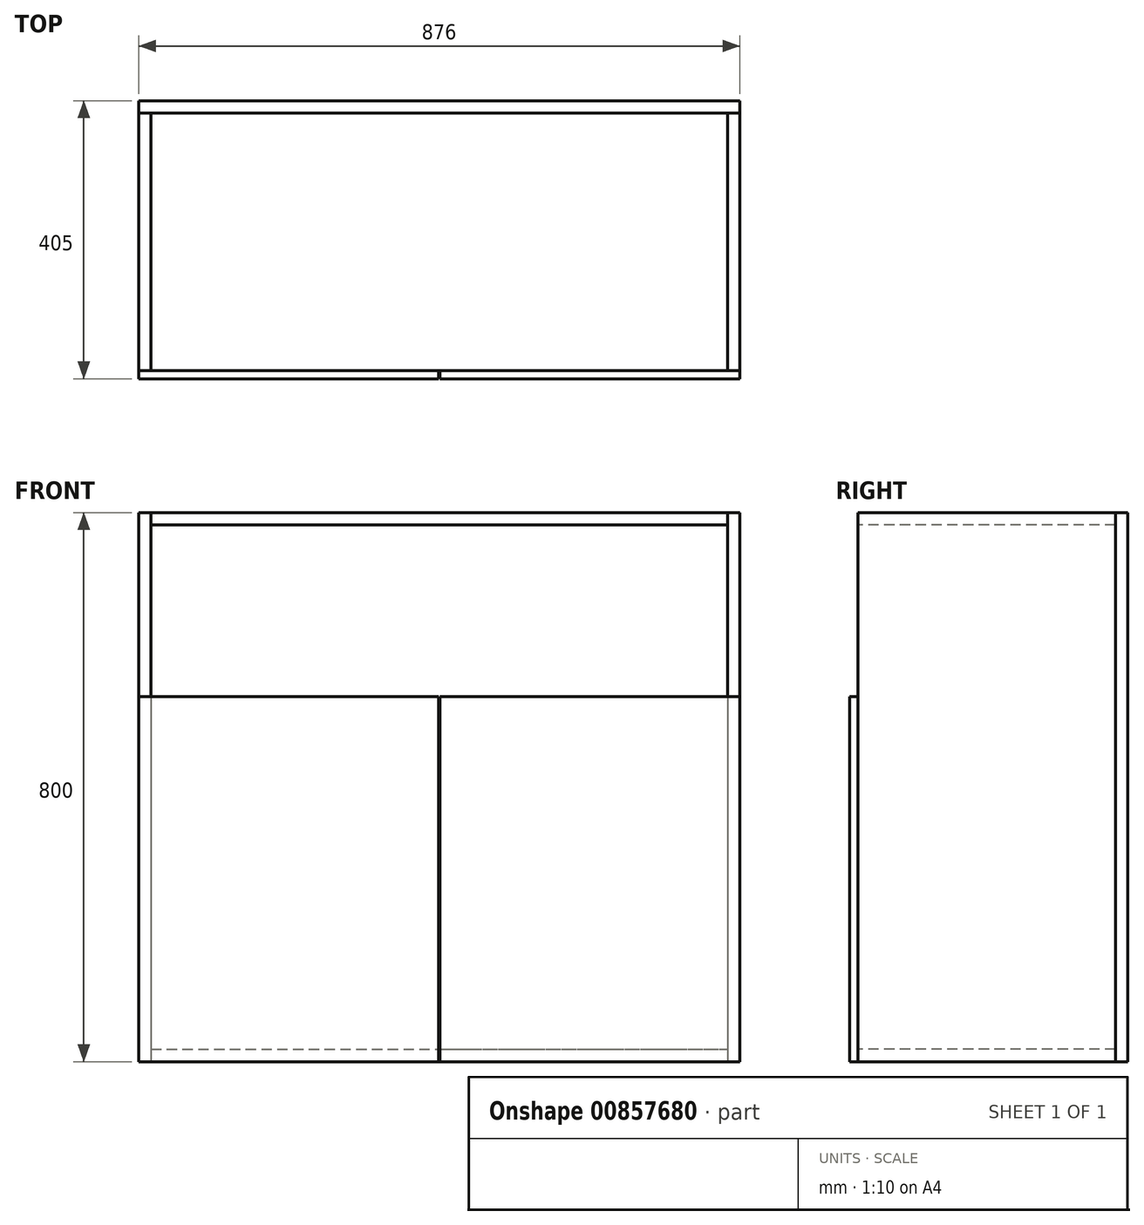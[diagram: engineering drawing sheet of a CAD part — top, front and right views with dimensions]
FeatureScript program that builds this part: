
annotation { "Feature Type Name" : "Feature", "Feature Type Description" : "" }
export const myFeature = defineFeature(function(context is Context, id is Id, definition is map)
    precondition{}
    {
        {
            var Q0;
            Q0=qCreatedBy(makeId("Top.planeOp"),FACE);
            var sketch = newSketch(context, id + "F0", { "sketchPlane" : qUnion([Q0])});
            skLineSegment(sketch, "E0.bottom", {"start": v(438, -187.5) * mm, "end": v(-438, -187.5) * mm});
            skLineSegment(sketch, "E0.top", {"start": v(438, 187.5) * mm, "end": v(-438, 187.5) * mm});
            skLineSegment(sketch, "E0.left", {"start": v(438, -187.5) * mm, "end": v(438, 187.5) * mm});
            skLineSegment(sketch, "E0.right", {"start": v(-438, -187.5) * mm, "end": v(-438, 187.5) * mm});
            skPoint(sketch, "E0.middle", {"position": v(0, 0) * mm});
            skLineSegment(sketch, "E1.0", {"start": v(420, 169.5) * mm, "end": v(-420, 169.5) * mm});
            skLineSegment(sketch, "E1.1", {"start": v(420, -169.5) * mm, "end": v(420, 169.5) * mm});
            skLineSegment(sketch, "E1.2", {"start": v(420, -169.5) * mm, "end": v(-420, -169.5) * mm});
            skLineSegment(sketch, "E1.3", {"start": v(-420, -169.5) * mm, "end": v(-420, 169.5) * mm});
            skLineSegment(sketch, "E2", {"start": v(-420, -169.5) * mm, "end": v(-420, -187.5) * mm});
            skLineSegment(sketch, "E3", {"start": v(-420, 169.5) * mm, "end": v(-420, 187.5) * mm});
            skLineSegment(sketch, "E4", {"start": v(420, 169.5) * mm, "end": v(420, 187.5) * mm});
            skLineSegment(sketch, "E5", {"start": v(420, -169.5) * mm, "end": v(420, -187.5) * mm});
            skSolve(sketch);
        }
        {
            var Q0;
            {var subQ0=sQuery(id+"F0.wireOp",EDGE,"E0.right");Q0=makeQuery(id+"F0.imprint","IMPRINT",FACE,{"disambiguationData":[TD([[makeQuery(id+"F0.imprint","IMPRINT",EDGE,{"derivedFrom":subQ0}),-1.0]])]});}
            var Q1;
            {var subQ0=sQuery(id+"F0.wireOp",EDGE,"E0.left");Q1=makeQuery(id+"F0.imprint","IMPRINT",FACE,{"disambiguationData":[TD([[makeQuery(id+"F0.imprint","IMPRINT",EDGE,{"derivedFrom":subQ0}),1.0]])]});}
            extrude(context, id + "F1", {"entities" : qUnion([Q0, Q1]), "depth" : 800 * mm, "offsetDistance" : 25 * mm});
        }
        {
            var Q0;
            Q0=makeQuery(id+"F1.opExtrude","CAP_FACE",FACE,{"disambiguationData":[OSD([sQuery(id+"F0.wireOp",EDGE,"E0.bottom"),sQuery(id+"F0.wireOp",EDGE,"E0.top"),sQuery(id+"F0.wireOp",EDGE,"E0.right"),sQuery(id+"F0.wireOp",EDGE,"E1.3"),sQuery(id+"F0.wireOp",EDGE,"E2"),sQuery(id+"F0.wireOp",EDGE,"E3")])],"isStart":false});
            var sketch = newSketch(context, id + "F2", { "sketchPlane" : qUnion([Q0])});
            skLineSegment(sketch, "E6.bottom", {"start": v(-420, -187.5) * mm, "end": v(420, -187.5) * mm});
            skLineSegment(sketch, "E6.top", {"start": v(-420, 187.5) * mm, "end": v(420, 187.5) * mm});
            skLineSegment(sketch, "E6.left", {"start": v(-420, -187.5) * mm, "end": v(-420, 187.5) * mm});
            skLineSegment(sketch, "E6.right", {"start": v(420, -187.5) * mm, "end": v(420, 187.5) * mm});
            skSolve(sketch);
        }
        {
            var Q0;
            Q0=makeQuery(id+"F2.imprint","IMPRINT",FACE,{"disambiguationData":[TD([[makeQuery(id+"F2.imprint","IMPRINT",EDGE,{"derivedFrom":sQuery(id+"F2.wireOp",EDGE,"E6.bottom")}),1.0]])]});
            extrude(context, id + "F3", {"entities" : qUnion([Q0]), "oppositeDirection" : true, "depth" : 18 * mm, "offsetDistance" : 25 * mm});
        }
        {
            var Q0;
            {var subQ0=sQuery(id+"F0.wireOp",EDGE,"E0.right");Q0=makeQuery(id+"F0.imprint","IMPRINT",FACE,{"disambiguationData":[TD([[makeQuery(id+"F0.imprint","IMPRINT",EDGE,{"derivedFrom":subQ0}),-1.0]])]});}
            var sketch = newSketch(context, id + "F4", { "sketchPlane" : qUnion([Q0])});
            skLineSegment(sketch, "E7.bottom", {"start": v(-420, -187.5) * mm, "end": v(420, -187.5) * mm});
            skLineSegment(sketch, "E7.top", {"start": v(-420, 187.5) * mm, "end": v(420, 187.5) * mm});
            skLineSegment(sketch, "E7.left", {"start": v(-420, -187.5) * mm, "end": v(-420, 187.5) * mm});
            skLineSegment(sketch, "E7.right", {"start": v(420, -187.5) * mm, "end": v(420, 187.5) * mm});
            skSolve(sketch);
        }
        {
            var Q0;
            {var subQ6=sQuery(id+"F4.wireOp",EDGE,"E7.bottom");Q0=makeQuery(id+"F4.imprint","IMPRINT",FACE,{"disambiguationData":[TD([[makeQuery(id+"F4.imprint","IMPRINT",EDGE,{"derivedFrom":subQ6}),1.0]])]});}
            extrude(context, id + "F5", {"entities" : qUnion([Q0]), "depth" : 18 * mm, "offsetDistance" : 25 * mm});
        }
        {
            var Q0;
            Q0=makeQuery(id+"F3.opExtrude","SWEPT_FACE",FACE,{"disambiguationData":[OSD([sQuery(id+"F2.wireOp",EDGE,"E6.top")])]});
            var sketch = newSketch(context, id + "F6", { "sketchPlane" : qUnion([Q0])});
            skLineSegment(sketch, "E8.bottom", {"start": v(-438, 800) * mm, "end": v(438, 800) * mm});
            skLineSegment(sketch, "E8.top", {"start": v(-438, 0) * mm, "end": v(438, 0) * mm});
            skLineSegment(sketch, "E8.left", {"start": v(-438, 800) * mm, "end": v(-438, 0) * mm});
            skLineSegment(sketch, "E8.right", {"start": v(438, 800) * mm, "end": v(438, 0) * mm});
            skSolve(sketch);
        }
        {
            var Q0;
            Q0=makeQuery(id+"F6.imprint","IMPRINT",FACE,{"disambiguationData":[TD([[makeQuery(id+"F6.imprint","IMPRINT",EDGE,{"derivedFrom":sQuery(id+"F6.wireOp",EDGE,"E8.top")}),1.0]])]});
            var Q1;
            {var subQ1=sQuery(id+"F2.wireOp",EDGE,"E6.top");Q1=makeQuery(id+"F6.imprint","IMPRINT",FACE,{"disambiguationData":[TD([[makeQuery(id+"F6.imprint","IMPRINT",EDGE,{"derivedFrom":makeQuery(id+"F3.opExtrude","CAP_EDGE",EDGE,{"disambiguationData":[OSD([subQ1])],"isStart":false})}),-1.0]])]});}
            extrude(context, id + "F7", {"entities" : qUnion([Q0, Q1]), "depth" : 18 * mm, "offsetDistance" : 25 * mm});
        }
        {
            var Q0;
            {var subQ0=sQuery(id+"F0.wireOp",EDGE,"E0.bottom");Q0=makeQuery(id+"F1.opExtrude","SWEPT_FACE",FACE,{"disambiguationData":[OSD([subQ0]),TDD([makeQuery(id+"F0.imprint","IMPRINT",EDGE,{"disambiguationData":[TD([[makeQuery(id+"F0.imprint","INTERSECT",VERTEX,{"derivedFrom":[subQ0,sQuery(id+"F0.wireOp",EDGE,"E0.right")]}),1.0]])],"derivedFrom":subQ0})])]});}
            var sketch = newSketch(context, id + "F8", { "sketchPlane" : qUnion([Q0])});
            skLineSegment(sketch, "E9.bottom", {"start": v(-438, 0) * mm, "end": v(-1, 0) * mm});
            skLineSegment(sketch, "E9.top", {"start": v(-438, 532) * mm, "end": v(-1, 532) * mm});
            skLineSegment(sketch, "E9.left", {"start": v(-438, 0) * mm, "end": v(-438, 532) * mm});
            skLineSegment(sketch, "E9.right", {"start": v(-1, 0) * mm, "end": v(-1, 532) * mm});
            skLineSegment(sketch, "E10.bottom", {"start": v(438, 0) * mm, "end": v(1, 0) * mm});
            skLineSegment(sketch, "E10.top", {"start": v(438, 532) * mm, "end": v(1, 532) * mm});
            skLineSegment(sketch, "E10.left", {"start": v(438, 0) * mm, "end": v(438, 532) * mm});
            skLineSegment(sketch, "E10.right", {"start": v(1, 0) * mm, "end": v(1, 532) * mm});
            skSolve(sketch);
        }
        {
            var Q0;
            {var subQ3=sQuery(id+"F8.wireOp",EDGE,"E9.right");Q0=makeQuery(id+"F8.imprint","IMPRINT",FACE,{"disambiguationData":[TD([[makeQuery(id+"F8.imprint","IMPRINT",EDGE,{"derivedFrom":subQ3}),1.0]])]});}
            var Q1;
            {var subQ0=sQuery(id+"F8.wireOp",EDGE,"E9.left");Q1=makeQuery(id+"F8.imprint","IMPRINT",FACE,{"disambiguationData":[TD([[makeQuery(id+"F8.imprint","IMPRINT",EDGE,{"derivedFrom":subQ0}),1.0]])]});}
            var Q2;
            Q2=makeQuery(id+"F8.imprint","IMPRINT",FACE,{"disambiguationData":[TD([[makeQuery(id+"F8.imprint","IMPRINT",EDGE,{"derivedFrom":sQuery(id+"F8.wireOp",EDGE,"E10.bottom")}),-1.0]])]});
            extrude(context, id + "F9", {"entities" : qUnion([Q0, Q1, Q2]), "depth" : 12 * mm, "offsetDistance" : 25 * mm});
        }
        {
            var Q0;
            Q0=makeQuery(id+"F1.opExtrude","SWEPT_FACE",FACE,{"disambiguationData":[OSD([sQuery(id+"F0.wireOp",EDGE,"E0.left")])]});
            var sketch = newSketch(context, id + "F10", { "sketchPlane" : qUnion([Q0])});
            skLineSegment(sketch, "E11.bottom", {"start": v(205.5, 0) * mm, "end": v(-199.5, 0) * mm});
            skLineSegment(sketch, "E11.top", {"start": v(205.5, 800) * mm, "end": v(-199.5, 800) * mm});
            skLineSegment(sketch, "E11.left", {"start": v(205.5, 0) * mm, "end": v(205.5, 800) * mm});
            skLineSegment(sketch, "E11.right", {"start": v(-199.5, 0) * mm, "end": v(-199.5, 800) * mm});
            skSolve(sketch);
        }
        {
            var Q0;
            {var subQ1=sQuery(id+"F0.wireOp",EDGE,"E0.left");var subQ2=makeQuery(id+"F1.opExtrude","SWEPT_EDGE",EDGE,{"disambiguationData":[OSD([sQuery(id+"F0.wireOp",EDGE,"E0.bottom"),subQ1])]});Q0=makeQuery(id+"F10.imprint","IMPRINT",FACE,{"disambiguationData":[TD([[makeQuery(id+"F10.imprint","IMPRINT",EDGE,{"derivedFrom":subQ2}),1.0]])]});}
            extrude(context, id + "F11", {"entities" : qUnion([Q0]), "depth" : 12 * mm, "offsetDistance" : 25 * mm});
        }
        {
            var Q0;
            Q0=makeQuery(id+"F11.opExtrude","SWEPT_BODY",BODY,{"disambiguationData":[OSD([sQuery(id+"F0.wireOp",EDGE,"E0.bottom"),sQuery(id+"F0.wireOp",EDGE,"E0.top"),sQuery(id+"F0.wireOp",EDGE,"E0.left"),sQuery(id+"F10.wireOp",EDGE,"E11.bottom"),sQuery(id+"F10.wireOp",EDGE,"E11.top")])]});
            deleteBodies(context, id + "F12", {"entities" : qUnion([Q0])});
        }
    });
